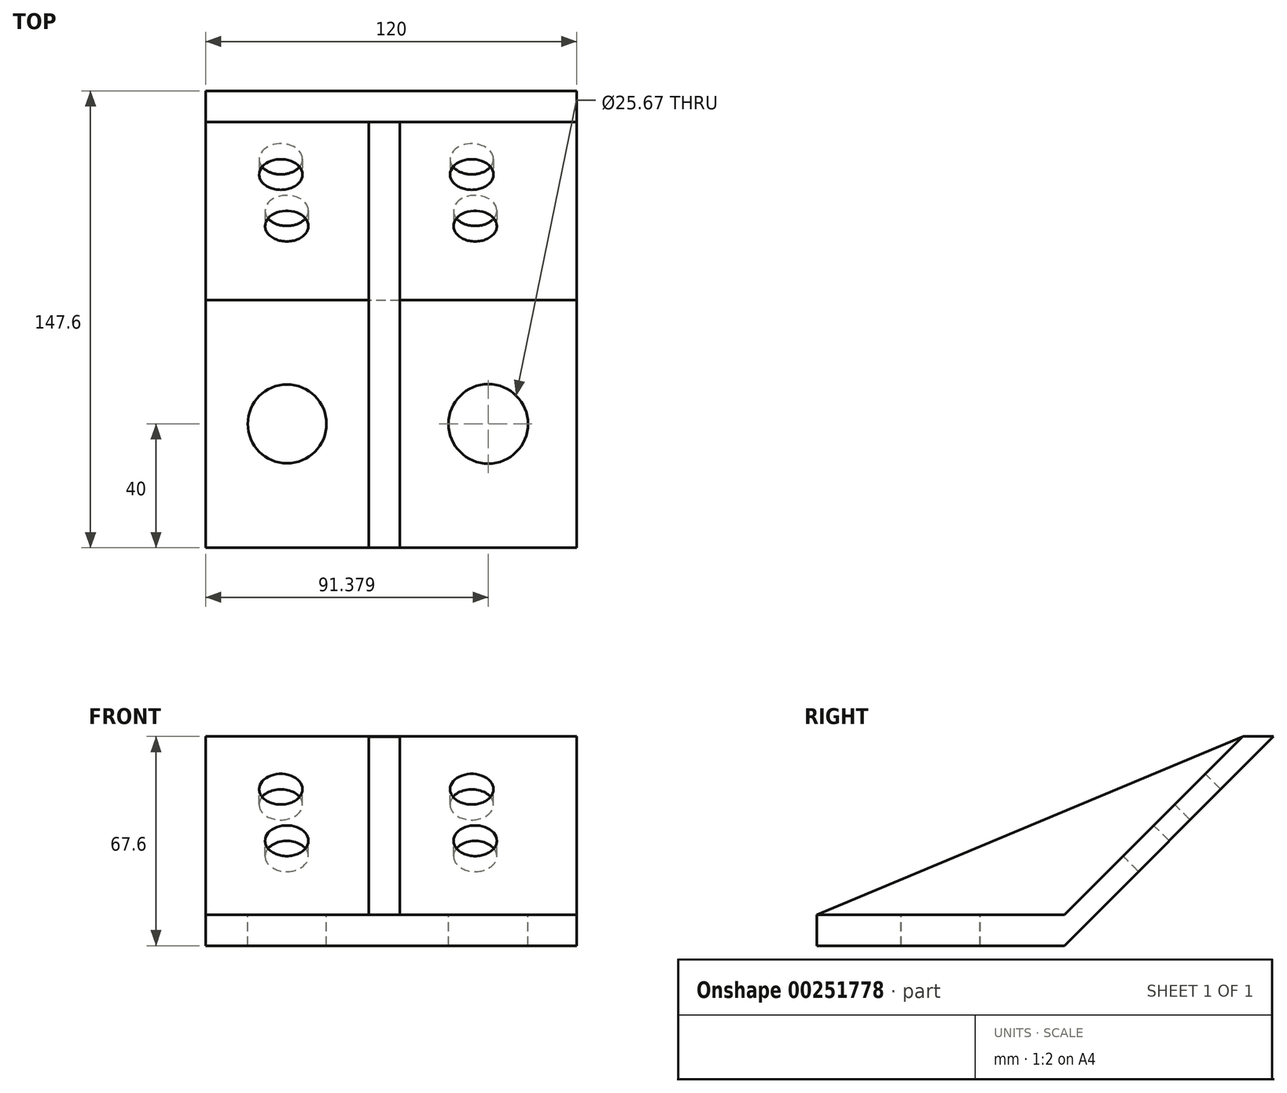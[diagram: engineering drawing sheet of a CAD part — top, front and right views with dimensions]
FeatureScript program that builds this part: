
annotation { "Feature Type Name" : "Feature", "Feature Type Description" : "" }
export const myFeature = defineFeature(function(context is Context, id is Id, definition is map)
    precondition{}
    {
        {
            var Q0;
            Q0=qCreatedBy(makeId("Right.planeOp"),FACE);
            var sketch = newSketch(context, id + "F0", { "sketchPlane" : qUnion([Q0])});
            skLineSegment(sketch, "E0.bottom", {"start": v(-40, -5) * mm, "end": v(40, -5) * mm});
            skLineSegment(sketch, "E0.top", {"start": v(-40, 5) * mm, "end": v(40, 5) * mm});
            skLineSegment(sketch, "E0.left", {"start": v(-40, -5) * mm, "end": v(-40, 5) * mm});
            skLineSegment(sketch, "E0.right", {"start": v(40, -5) * mm, "end": v(40, 5) * mm});
            skPoint(sketch, "E0.middle", {"position": v(0, 0) * mm});
            skLineSegment(sketch, "E1", {"start": v(40, 5) * mm, "end": v(97.6, 62.6) * mm});
            skLineSegment(sketch, "E2", {"start": v(97.6, 62.6) * mm, "end": v(107.6, 62.6) * mm});
            skLineSegment(sketch, "E3", {"start": v(107.6, 62.6) * mm, "end": v(40, -5) * mm});
            skSolve(sketch);
        }
        {
            var Q0;
            Q0 = qSketchRegion(id + "F0", true);
            extrude(context, id + "F1", {"entities" : qUnion([Q0]), "endBound" : BoundingType.SYMMETRIC, "oppositeDirection" : true, "depth" : 120 * mm});
        }
        {
            var Q0;
            Q0=qCreatedBy(makeId("Top.planeOp"),FACE);
            var sketch = newSketch(context, id + "F2", { "sketchPlane" : qUnion([Q0])});
            skLineSegment(sketch, "E4.bottom", {"start": v(-7.24, 97.6) * mm, "end": v(2.76, 97.6) * mm});
            skLineSegment(sketch, "E4.top", {"start": v(-7.24, -40) * mm, "end": v(2.76, -40) * mm});
            skLineSegment(sketch, "E4.left", {"start": v(-7.24, 97.6) * mm, "end": v(-7.24, -40) * mm});
            skLineSegment(sketch, "E4.right", {"start": v(2.76, 97.6) * mm, "end": v(2.76, -40) * mm});
            skSolve(sketch);
        }
        {
            var Q0;
            Q0 = qSketchRegion(id + "F2", true);
            extrude(context, id + "F3", {"entities" : qUnion([Q0]), "operationType" : NewBodyOperationType.ADD, "depth" : 62.5 * mm});
        }
        {
            var Q0;
            {var subQ0=sQuery(id+"F2.wireOp",EDGE,"E4.right");Q0=makeQuery(id+"F3.boolean.opBoolean","SPLIT",FACE,{"disambiguationData":[TD([makeQuery(id+"F1.opExtrude","SWEPT_FACE",FACE,{"disambiguationData":[OSD([sQuery(id+"F0.wireOp",EDGE,"E0.top")])]})])],"derivedFrom":makeQuery(id+"F3.opExtrude","SWEPT_FACE",FACE,{"disambiguationData":[OSD([subQ0])]})});}
            var sketch = newSketch(context, id + "F4", { "sketchPlane" : qUnion([Q0])});
            skLineSegment(sketch, "E5", {"start": v(-40, 5) * mm, "end": v(97.5, 62.5) * mm});
            skLineSegment(sketch, "E6.0.2", {"start": v(97.5, 62.5) * mm, "end": v(-40, 62.5) * mm});
            skLineSegment(sketch, "E6.0.3", {"start": v(-40, 62.5) * mm, "end": v(-40, 5) * mm});
            skPoint(sketch, "E6.0.1.start.orphan", {"position": v(40, 5) * mm});
            skSolve(sketch);
        }
        {
            var Q0;
            Q0 = qSketchRegion(id + "F4", true);
            extrude(context, id + "F5", {"entities" : qUnion([Q0]), "operationType" : NewBodyOperationType.REMOVE, "oppositeDirection" : true, "depth" : 25 * mm});
        }
        {
            var Q0;
            {var subQ1=sQuery(id+"F2.wireOp",EDGE,"E4.right");Q0=makeQuery(id+"F3.boolean.opBoolean","SPLIT",FACE,{"disambiguationData":[TD([makeQuery(id+"F1.opExtrude","SWEPT_FACE",FACE,{"disambiguationData":[OSD([sQuery(id+"F0.wireOp",EDGE,"E3")])]})])],"derivedFrom":makeQuery(id+"F3.opExtrude","SWEPT_FACE",FACE,{"disambiguationData":[OSD([subQ1])]})});}
            var sketch = newSketch(context, id + "F6", { "sketchPlane" : qUnion([Q0])});
            skSolve(sketch);
        }
        {
            var Q0;
            {var subQ0=sQuery(id+"F2.wireOp",EDGE,"E4.right");Q0=makeQuery(id+"F6.imprint","IMPRINT",FACE,{"disambiguationData":[TD([[makeQuery(id+"F6.imprint","IMPRINT",EDGE,{"derivedFrom":makeQuery(id+"F3.opExtrude","CAP_EDGE",EDGE,{"disambiguationData":[OSD([subQ0])],"isStart":true})}),-1.0]])]});}
            extrude(context, id + "F7", {"entities" : qUnion([Q0]), "operationType" : NewBodyOperationType.REMOVE, "oppositeDirection" : true, "depth" : 25 * mm});
        }
        {
            var Q0;
            Q0=makeQuery(id+"F1.opExtrude","SWEPT_FACE",FACE,{"disambiguationData":[OSD([sQuery(id+"F0.wireOp",EDGE,"E1")])]});
            var sketch = newSketch(context, id + "F8", { "sketchPlane" : qUnion([Q0])});
            skCircle(sketch, "E7", {"center": v(26.05, 89.2) * mm, "radius": 7 * mm});
            skCircle(sketch, "E8", {"center": v(27.14, 65.63) * mm, "radius": 7 * mm});
            skCircle(sketch, "E9", {"center": v(-35.65, 89.2) * mm, "radius": 7 * mm});
            skCircle(sketch, "E10", {"center": v(-33.74, 65.63) * mm, "radius": 7 * mm});
            skSolve(sketch);
        }
        {
            var Q0;
            Q0 = qSketchRegion(id + "F8", true);
            extrude(context, id + "F9", {"entities" : qUnion([Q0]), "operationType" : NewBodyOperationType.REMOVE, "endBound" : BoundingType.THROUGH_ALL, "oppositeDirection" : true, "depth" : 25 * mm});
        }
        {
            var Q0;
            {var subQ2=sQuery(id+"F0.wireOp",EDGE,"E0.top");Q0=makeQuery(id+"F3.boolean.opBoolean","SPLIT",FACE,{"disambiguationData":[TD([makeQuery(id+"F3.opExtrude","SWEPT_FACE",FACE,{"disambiguationData":[OSD([sQuery(id+"F2.wireOp",EDGE,"E4.right")])]})])],"derivedFrom":makeQuery(id+"F1.opExtrude","SWEPT_FACE",FACE,{"disambiguationData":[OSD([subQ2])]})});}
            var sketch = newSketch(context, id + "F10", { "sketchPlane" : qUnion([Q0])});
            skCircle(sketch, "E11", {"center": v(31.38, 0) * mm, "radius": 12.84 * mm});
            skPoint(sketch, "E11.centerSnap0", {"position": v(31.38, 40) * mm});
            skSolve(sketch);
        }
        {
            var Q0;
            Q0 = qSketchRegion(id + "F10", true);
            extrude(context, id + "F11", {"entities" : qUnion([Q0]), "operationType" : NewBodyOperationType.REMOVE, "endBound" : BoundingType.THROUGH_ALL, "oppositeDirection" : true, "depth" : 25 * mm});
        }
        {
            var Q0;
            {var subQ2=sQuery(id+"F0.wireOp",EDGE,"E0.top");Q0=makeQuery(id+"F3.boolean.opBoolean","SPLIT",FACE,{"disambiguationData":[TD([makeQuery(id+"F3.opExtrude","SWEPT_FACE",FACE,{"disambiguationData":[OSD([sQuery(id+"F2.wireOp",EDGE,"E4.left")])]})])],"derivedFrom":makeQuery(id+"F1.opExtrude","SWEPT_FACE",FACE,{"disambiguationData":[OSD([subQ2])]})});}
            var sketch = newSketch(context, id + "F12", { "sketchPlane" : qUnion([Q0])});
            skCircle(sketch, "E12", {"center": v(-33.62, 0) * mm, "radius": 12.72 * mm});
            skPoint(sketch, "E12.centerSnap0", {"position": v(-33.62, 40) * mm});
            skSolve(sketch);
        }
        {
            var Q0;
            Q0 = qSketchRegion(id + "F12", true);
            extrude(context, id + "F13", {"entities" : qUnion([Q0]), "operationType" : NewBodyOperationType.REMOVE, "endBound" : BoundingType.THROUGH_ALL, "oppositeDirection" : true, "depth" : 25 * mm});
        }
    });
